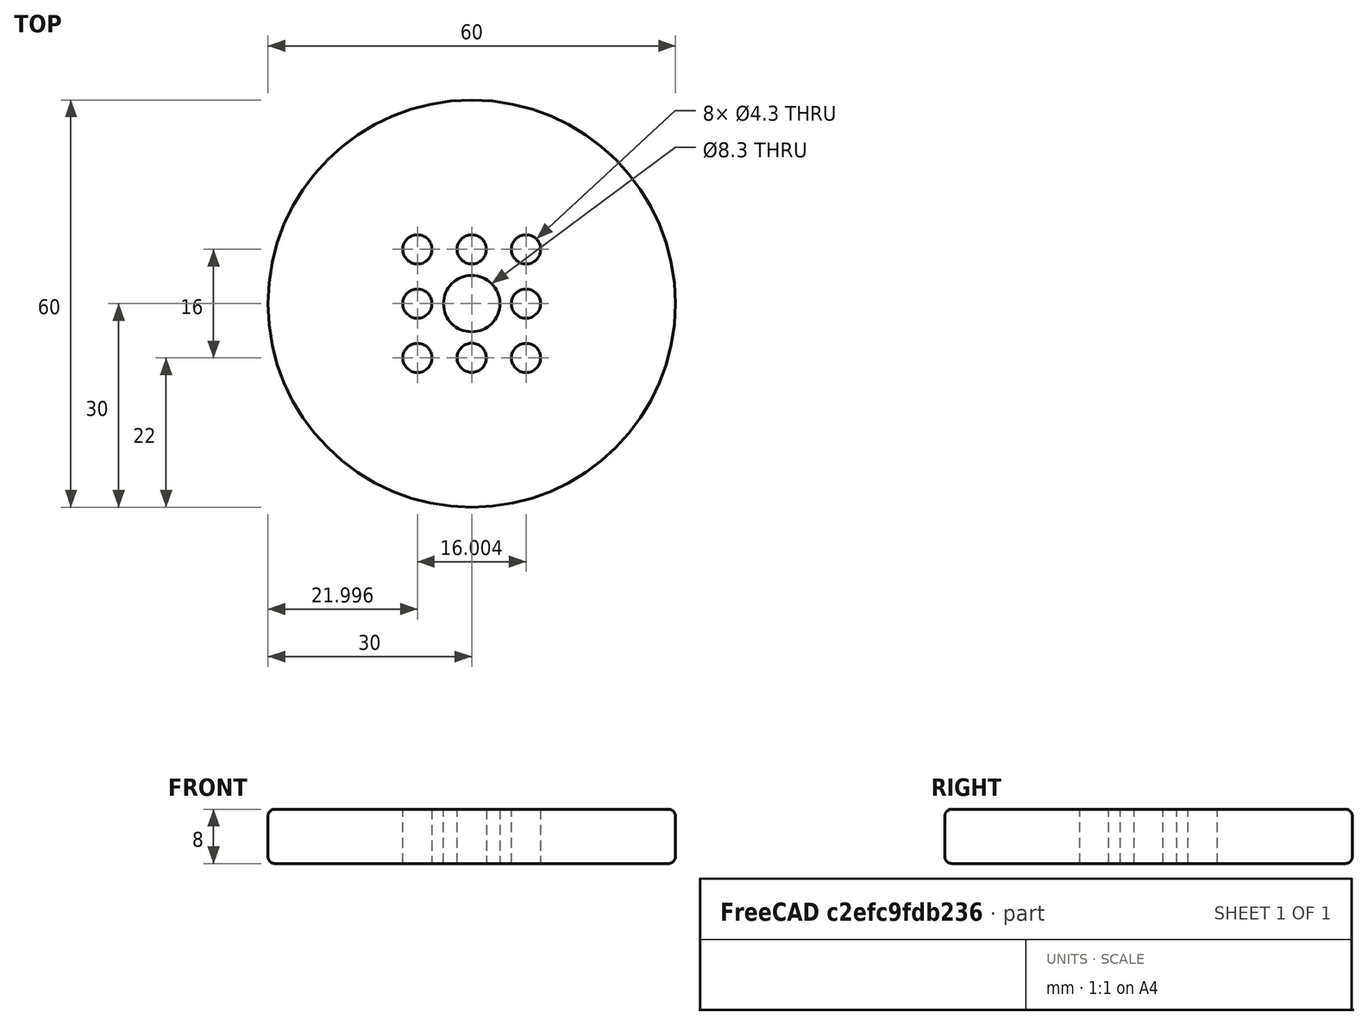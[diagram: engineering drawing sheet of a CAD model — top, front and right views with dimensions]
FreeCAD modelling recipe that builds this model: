
FCSTD DOCUMENT  (FreeCAD 0.21R33675 (Git))
Label: custom spinner thing
License: All rights reserved
LicenseURL: http://en.wikipedia.org/wiki/All_rights_reserved
objects: Sketcher::SketchObject×2, PartDesign::Fillet×2, Mesh::Feature×1, PartDesign::Pad×1, PartDesign::Pocket×1, PartDesign::Body×1
note: 11 computed .brp shape members not serialized (recipe doc carries the construction recipe); baked Part::Feature solids carry a one-line shape summary decoded from their .brp

FEATURE [Sketcher::SketchObject] Sketch
  FullyConstrained = true
  MapMode = 5
  Support = -> [XY_Plane]
  sketch-geometry (1):
    g0: Circle CenterX=0 CenterY=0 CenterZ=0 NormalX=0 NormalY=0 NormalZ=1 AngleXU=0 Radius=30
  constraints (2):
    c: Coincident(g0,g-1)
    c: Diameter(g0) = 60
FEATURE [Mesh::Feature] Unnamed_Plastic_Timing_Pulley_90T  label="Unnamed-Plastic Timing Pulley 90T"
  Placement = pos=(0,0,4.1) rot=(0,0,1;0rad)
FEATURE [PartDesign::Pad] Pad
  Direction = (0,0,1)
  Length = 8
  Length2 = 10
  Profile = -> Sketch
  ReferenceAxis = -> Sketch [N_Axis]
  Type = 0
FEATURE [Sketcher::SketchObject] Sketch001
  FullyConstrained = false
  MapMode = 5
  Placement = pos=(0,0,8) rot=(0,0,1;0rad)
  Support = -> [Pad]
  sketch-geometry (9):
    g0: Circle CenterX=0 CenterY=0 CenterZ=0 NormalX=0 NormalY=0 NormalZ=1 AngleXU=0 Radius=4.15
    g1: Circle CenterX=-8 CenterY=8 CenterZ=0 NormalX=0 NormalY=0 NormalZ=1 AngleXU=0 Radius=2.15
    g2: Circle CenterX=8 CenterY=8 CenterZ=0 NormalX=0 NormalY=0 NormalZ=1 AngleXU=0 Radius=2.15
    g3: Circle CenterX=8 CenterY=-8 CenterZ=0 NormalX=0 NormalY=0 NormalZ=1 AngleXU=0 Radius=2.15
    g4: Circle CenterX=-8 CenterY=-8 CenterZ=0 NormalX=0 NormalY=0 NormalZ=1 AngleXU=0 Radius=2.15
    g5: Circle CenterX=-8.00345 CenterY=0 CenterZ=0 NormalX=0 NormalY=0 NormalZ=1 AngleXU=0 Radius=2.15
    g6: Circle CenterX=7.99407 CenterY=0 CenterZ=0 NormalX=0 NormalY=0 NormalZ=1 AngleXU=0 Radius=2.15
    g7: Circle CenterX=0 CenterY=8 CenterZ=0 NormalX=0 NormalY=0 NormalZ=1 AngleXU=0 Radius=2.15
    g8: Circle CenterX=0 CenterY=-7.98628 CenterZ=0 NormalX=0 NormalY=0 NormalZ=1 AngleXU=0 Radius=2.15
  constraints (23):
    c: Coincident(g0,g-1)
    c: Diameter(g1) = 4.3
    c: Diameter(g2) = 4.3
    c: Diameter(g3) = 4.3
    c: Diameter(g4) = 4.3
    c: Diameter(g0) = 8.3
    c: PointOnObject(g5,g-1)
    c: PointOnObject(g6,g-1)
    c: PointOnObject(g7,g-2)
    c: PointOnObject(g8,g-2)
    c: Diameter(g7) = 4.3
    c: Diameter(g6) = 4.3
    c: Diameter(g8) = 4.3
    c: Diameter(g5) = 4.3
    c: DistanceX(g1,g7) = 8
    c: DistanceX(g7,g2) = 8
    c: DistanceY(g5,g1) = 8
    c: DistanceY(g6,g2) = 8
    c: DistanceX(g4,g8) = 8
    c: DistanceX(g8,g3) = 8
    c: DistanceY(g4,g5) = 8
    c: DistanceY(g3,g6) = 8
    c: DistanceY(g0,g7) = 8
FEATURE [PartDesign::Pocket] Pocket
  BaseFeature = -> Pad
  Direction = (0,0,-1)
  Length = 8
  Length2 = 5
  Profile = -> Sketch001
  ReferenceAxis = -> Sketch001 [N_Axis]
  Type = 0
FEATURE [PartDesign::Fillet] Fillet
  Base = -> Pocket [Edge3]
  BaseFeature = -> Pocket
  Radius = 1
  SupportTransform = false
  UseAllEdges = false
FEATURE [PartDesign::Fillet] Fillet001
  Base = -> Fillet [Edge3]
  BaseFeature = -> Fillet
  Radius = 1
  SupportTransform = false
  UseAllEdges = false
FEATURE [PartDesign::Body] Body  label="Spinner-Main"
  Group = -> [Sketch,Pad,Sketch001,Pocket,Fillet,Fillet001]
  Origin = -> Origin
  Tip = -> Fillet001
